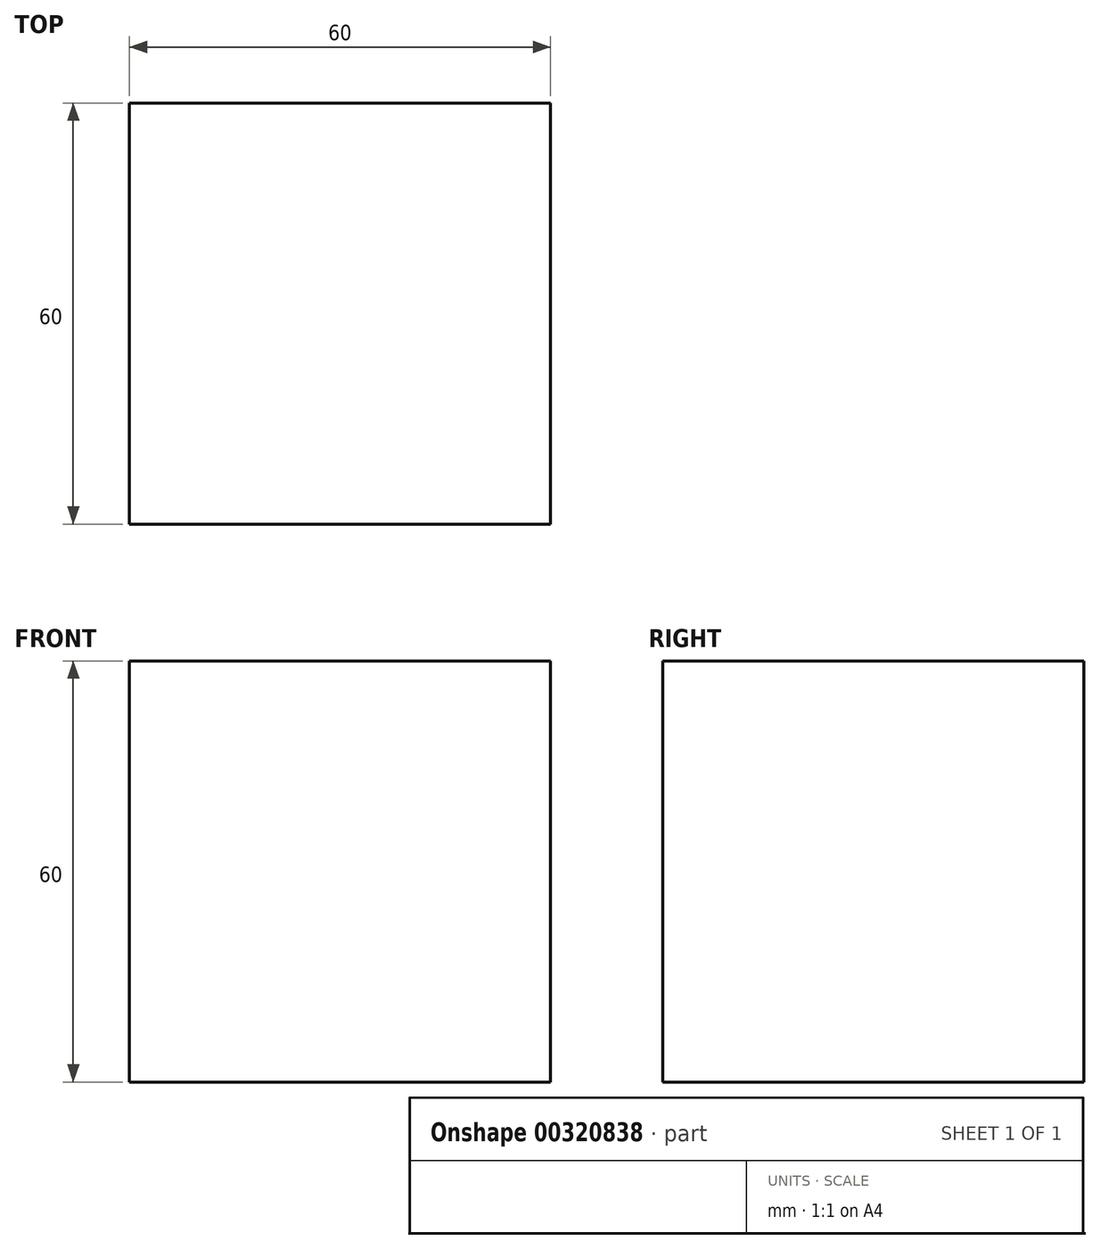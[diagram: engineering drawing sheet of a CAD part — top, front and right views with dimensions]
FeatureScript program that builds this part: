
annotation { "Feature Type Name" : "Feature", "Feature Type Description" : "" }
export const myFeature = defineFeature(function(context is Context, id is Id, definition is map)
    precondition{}
    {
        {
            var Q0;
            Q0=qCreatedBy(makeId("Front.planeOp"),FACE);
            var sketch = newSketch(context, id + "F0", { "sketchPlane" : qUnion([Q0])});
            skLineSegment(sketch, "E0.bottom", {"start": v(60, 60) * mm, "end": v(0, 60) * mm});
            skLineSegment(sketch, "E0.top", {"start": v(60, 0) * mm, "end": v(0, 0) * mm});
            skLineSegment(sketch, "E0.left", {"start": v(60, 60) * mm, "end": v(60, 0) * mm});
            skLineSegment(sketch, "E0.right", {"start": v(0, 60) * mm, "end": v(0, 0) * mm});
            skSolve(sketch);
        }
        {
            var Q0;
            Q0 = qSketchRegion(id + "F0", true);
            extrude(context, id + "F1", {"entities" : qUnion([Q0]), "depth" : 60 * mm});
        }
    });
